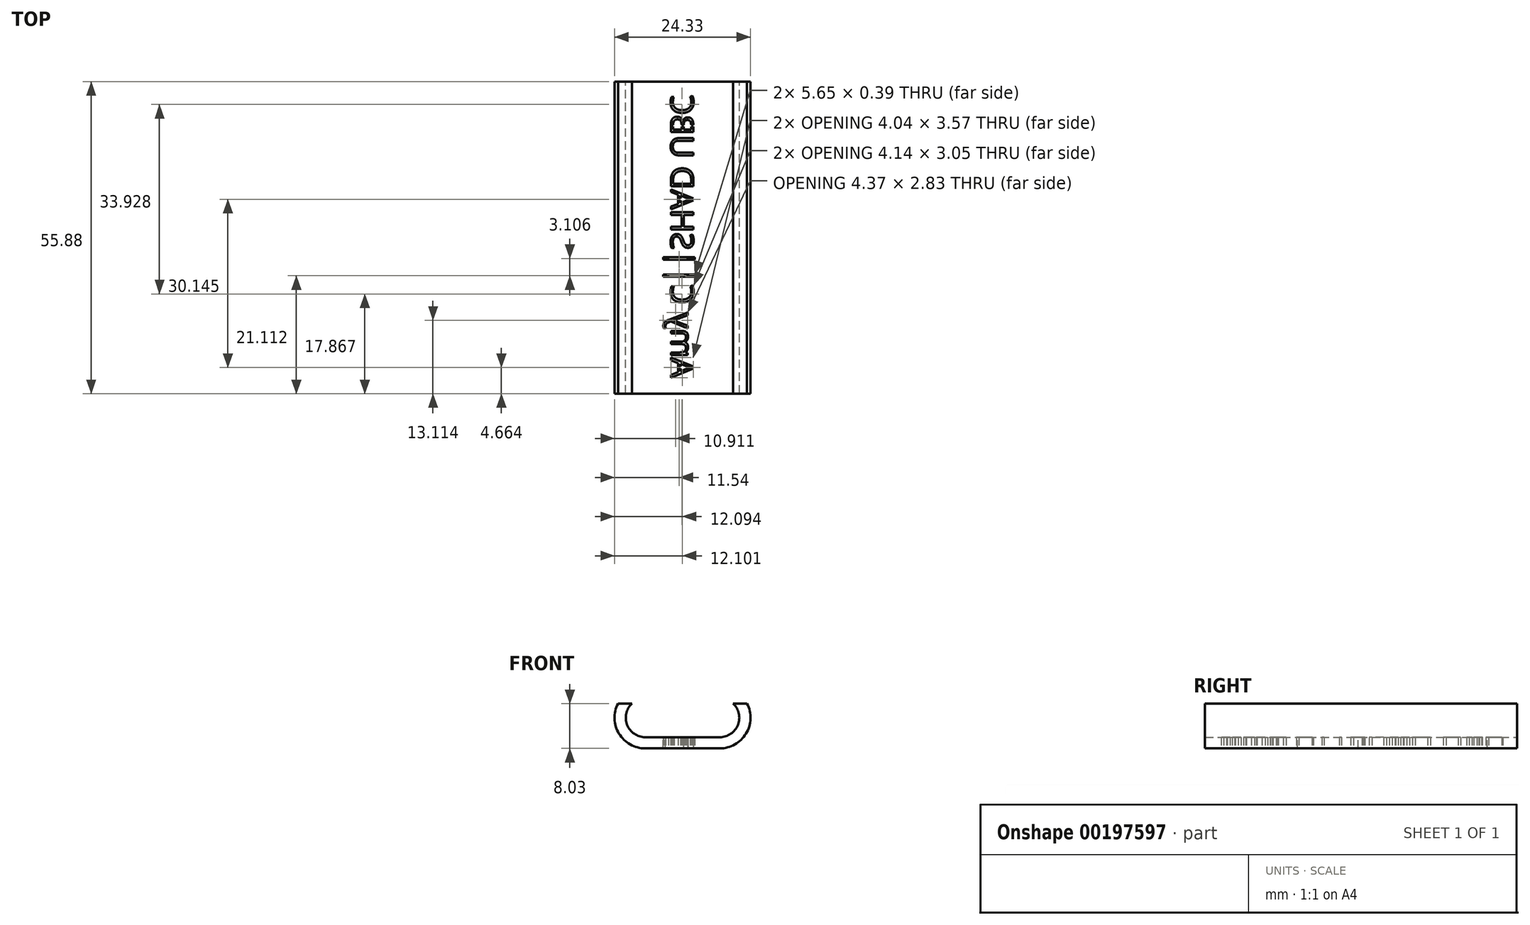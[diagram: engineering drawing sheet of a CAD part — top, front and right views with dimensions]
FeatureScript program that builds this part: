
annotation { "Feature Type Name" : "Feature", "Feature Type Description" : "" }
export const myFeature = defineFeature(function(context is Context, id is Id, definition is map)
    precondition{}
    {
        {
            var Q0;
            Q0=qCreatedBy(makeId("Front.planeOp"),FACE);
            var sketch = newSketch(context, id + "F0", { "sketchPlane" : qUnion([Q0])});
            skLineSegment(sketch, "E0.bottom", {"start": v(-6.36, 3.5) * mm, "end": v(6.97, 3.5) * mm});
            skLineSegment(sketch, "E0.top", {"start": v(-6.36, -3.48) * mm, "end": v(6.97, -3.48) * mm});
            skArc(sketch, "E1", {"start": v(6.97, -3.48) * mm, "mid": v(10.46, 0.01) * mm, "end": v(6.97, 3.5) * mm});
            skArc(sketch, "E2", {"start": v(-6.36, 3.5) * mm, "mid": v(-9.86, 0.01) * mm, "end": v(-6.36, -3.48) * mm});
            skLineSegment(sketch, "E3.0", {"start": v(-6.36, 5.51) * mm, "end": v(6.97, 5.51) * mm});
            skArc(sketch, "E3.1", {"start": v(-6.36, 5.51) * mm, "mid": v(-11.86, 0.01) * mm, "end": v(-6.36, -5.49) * mm});
            skLineSegment(sketch, "E3.2", {"start": v(-6.36, -5.49) * mm, "end": v(6.97, -5.49) * mm});
            skArc(sketch, "E3.3", {"start": v(6.97, -5.49) * mm, "mid": v(12.47, 0.01) * mm, "end": v(6.97, 5.51) * mm});
            skSolve(sketch);
        }
        {
            var Q0;
            Q0 = qSketchRegion(id + "F0", true);
            extrude(context, id + "F1", {"entities" : qUnion([Q0]), "depth" : 55.88 * mm});
        }
        {
            var Q0;
            Q0=makeQuery(id+"F1.opExtrude","CAP_FACE",FACE,{"disambiguationData":[OSD([sQuery(id+"F0.wireOp",EDGE,"E0.bottom"),sQuery(id+"F0.wireOp",EDGE,"E0.top"),sQuery(id+"F0.wireOp",EDGE,"E1"),sQuery(id+"F0.wireOp",EDGE,"E2"),sQuery(id+"F0.wireOp",EDGE,"E3.0"),sQuery(id+"F0.wireOp",EDGE,"E3.1"),sQuery(id+"F0.wireOp",EDGE,"E3.2"),sQuery(id+"F0.wireOp",EDGE,"E3.3")])],"isStart":false});
            var sketch = newSketch(context, id + "F2", { "sketchPlane" : qUnion([Q0])});
            skLineSegment(sketch, "E4.bottom", {"start": v(-14.7, 10.63) * mm, "end": v(17.44, 10.63) * mm});
            skLineSegment(sketch, "E4.top", {"start": v(-14.7, 2.54) * mm, "end": v(17.44, 2.54) * mm});
            skLineSegment(sketch, "E4.left", {"start": v(-14.7, 10.63) * mm, "end": v(-14.7, 2.54) * mm});
            skLineSegment(sketch, "E4.right", {"start": v(17.44, 10.63) * mm, "end": v(17.44, 2.54) * mm});
            skSolve(sketch);
        }
        {
            var Q0;
            Q0=makeQuery(id+"F2.imprint","IMPRINT",FACE,{"disambiguationData":[TD([[makeQuery(id+"F2.imprint","IMPRINT",EDGE,{"derivedFrom":sQuery(id+"F2.wireOp",EDGE,"E4.bottom")}),-1.0]])]});
            var Q1;
            {var subQ6=makeQuery(id+"F1.opExtrude","CAP_EDGE",EDGE,{"disambiguationData":[OSD([sQuery(id+"F0.wireOp",EDGE,"E0.bottom")])],"isStart":false});Q1=makeQuery(id+"F2.imprint","IMPRINT",FACE,{"disambiguationData":[TD([[makeQuery(id+"F2.imprint","IMPRINT",EDGE,{"derivedFrom":subQ6}),1.0]])]});}
            extrude(context, id + "F3", {"entities" : qUnion([Q0, Q1]), "operationType" : NewBodyOperationType.REMOVE, "oppositeDirection" : true, "depth" : 55.88 * mm});
        }
        {
            var Q0;
            Q0=makeQuery(id+"F1.opExtrude","SWEPT_FACE",FACE,{"disambiguationData":[OSD([sQuery(id+"F0.wireOp",EDGE,"E3.2")])]});
            var sketch = newSketch(context, id + "F4", { "sketchPlane" : qUnion([Q0])});
            skText(sketch, "E5", { "text": "Amy C||SHAD UBC", "fontName": "OpenSans-Regular.ttf"});
            const initialGuessF4  = {"E5": [-0.00178, 0.053, 0, -1, 0.00406]};
            skSetInitialGuess(sketch, initialGuessF4);
            skSolve(sketch);
        }
        {
            var Q0;
            Q0 = qSketchRegion(id + "F4", true);
            extrude(context, id + "F5", {"entities" : qUnion([Q0]), "operationType" : NewBodyOperationType.REMOVE, "oppositeDirection" : true, "depth" : 12.7 * mm});
        }
        {
            var Q0;
            {var subQ1=sQuery(id+"F0.wireOp",EDGE,"E3.1");var subQ2=sQuery(id+"F0.wireOp",EDGE,"E3.2");Q0=makeQuery(id+"F5.boolean.opBoolean","SPLIT",FACE,{"disambiguationData":[TD([makeQuery(id+"F1.opExtrude","SWEPT_FACE",FACE,{"disambiguationData":[OSD([subQ1])]})])],"derivedFrom":makeQuery(id+"F1.opExtrude","SWEPT_FACE",FACE,{"disambiguationData":[OSD([subQ2])]})});}
            var sketch = newSketch(context, id + "F6", { "sketchPlane" : qUnion([Q0])});
            skLineSegment(sketch, "E6.bottom", {"start": v(2.26, -51.41) * mm, "end": v(-0.47, -51.41) * mm});
            skLineSegment(sketch, "E6.top", {"start": v(2.26, -51.03) * mm, "end": v(-0.47, -51.03) * mm});
            skLineSegment(sketch, "E6.left", {"start": v(2.26, -51.41) * mm, "end": v(2.26, -51.03) * mm});
            skLineSegment(sketch, "E6.right", {"start": v(-0.47, -51.41) * mm, "end": v(-0.47, -51.03) * mm});
            skLineSegment(sketch, "E7.bottom", {"start": v(2.26, -51.41) * mm, "end": v(-0.48, -51.41) * mm});
            skLineSegment(sketch, "E7.top", {"start": v(2.26, -50.98) * mm, "end": v(-0.48, -50.98) * mm});
            skLineSegment(sketch, "E7.left", {"start": v(2.26, -51.41) * mm, "end": v(2.26, -50.98) * mm});
            skLineSegment(sketch, "E7.right", {"start": v(-0.48, -51.41) * mm, "end": v(-0.48, -50.98) * mm});
            skLineSegment(sketch, "E8.bottom", {"start": v(2.26, 51.4) * mm, "end": v(-0.5, 51.4) * mm});
            skLineSegment(sketch, "E8.top", {"start": v(2.26, 51.02) * mm, "end": v(-0.5, 51.02) * mm});
            skLineSegment(sketch, "E8.left", {"start": v(2.26, 51.4) * mm, "end": v(2.26, 51.02) * mm});
            skLineSegment(sketch, "E8.right", {"start": v(-0.5, 51.4) * mm, "end": v(-0.5, 51.02) * mm});
            skLineSegment(sketch, "E9.bottom", {"start": v(2.26, 21.27) * mm, "end": v(-0.5, 21.27) * mm});
            skLineSegment(sketch, "E9.top", {"start": v(2.26, 20.87) * mm, "end": v(-0.5, 20.87) * mm});
            skLineSegment(sketch, "E9.left", {"start": v(2.26, 21.27) * mm, "end": v(2.26, 20.87) * mm});
            skLineSegment(sketch, "E9.right", {"start": v(-0.5, 21.27) * mm, "end": v(-0.5, 20.87) * mm});
            skLineSegment(sketch, "E10.bottom", {"start": v(0.53, 18.74) * mm, "end": v(0.27, 18.74) * mm});
            skLineSegment(sketch, "E10.top", {"start": v(0.53, 15.52) * mm, "end": v(0.27, 15.52) * mm});
            skLineSegment(sketch, "E10.left", {"start": v(0.53, 18.74) * mm, "end": v(0.53, 15.52) * mm});
            skLineSegment(sketch, "E10.right", {"start": v(0.27, 18.74) * mm, "end": v(0.27, 15.52) * mm});
            skLineSegment(sketch, "E11.bottom", {"start": v(2.25, 8.06) * mm, "end": v(-1.78, 8.06) * mm});
            skLineSegment(sketch, "E11.top", {"start": v(2.25, 7.78) * mm, "end": v(-1.78, 7.78) * mm});
            skLineSegment(sketch, "E11.left", {"start": v(2.25, 8.06) * mm, "end": v(2.25, 7.78) * mm});
            skLineSegment(sketch, "E11.right", {"start": v(-1.78, 8.06) * mm, "end": v(-1.78, 7.78) * mm});
            skSolve(sketch);
        }
        {
            var Q0;
            Q0=makeQuery(id+"F6.imprint","IMPRINT",FACE,{"disambiguationData":[TD([[makeQuery(id+"F6.imprint","IMPRINT",EDGE,{"derivedFrom":sQuery(id+"F6.wireOp",EDGE,"E8.bottom")}),1.0]])]});
            var Q1;
            Q1=makeQuery(id+"F6.imprint","IMPRINT",FACE,{"disambiguationData":[TD([[makeQuery(id+"F6.imprint","IMPRINT",EDGE,{"derivedFrom":sQuery(id+"F6.wireOp",EDGE,"E9.bottom")}),1.0]])]});
            var Q2;
            {var subQ0=sQuery(id+"F6.wireOp",EDGE,"E10.bottom");Q2=makeQuery(id+"F6.imprint","IMPRINT",FACE,{"disambiguationData":[TD([[makeQuery(id+"F6.imprint","IMPRINT",EDGE,{"derivedFrom":subQ0}),-1.0]])]});}
            var Q3;
            {var subQ4=sQuery(id+"F6.wireOp",EDGE,"E11.bottom");Q3=makeQuery(id+"F6.imprint","IMPRINT",FACE,{"disambiguationData":[TD([[makeQuery(id+"F6.imprint","IMPRINT",EDGE,{"derivedFrom":subQ4}),1.0]])]});}
            extrude(context, id + "F7", {"entities" : qUnion([Q0, Q1, Q2, Q3]), "operationType" : NewBodyOperationType.ADD, "oppositeDirection" : true, "depth" : 2 * mm});
        }
    });
